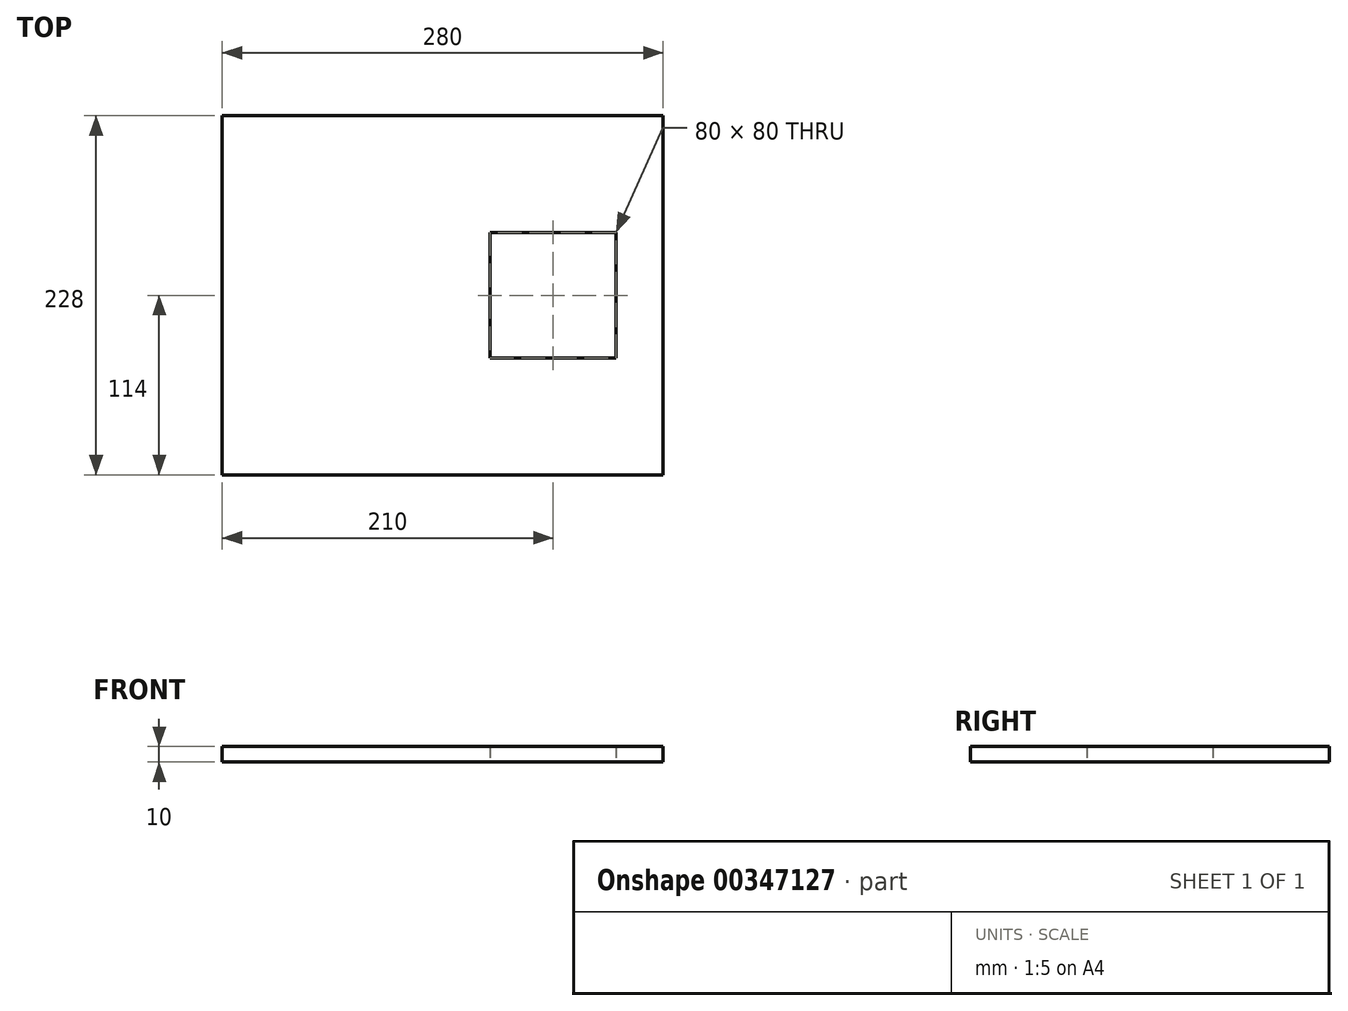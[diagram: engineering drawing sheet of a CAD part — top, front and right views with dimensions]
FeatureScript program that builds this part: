
annotation { "Feature Type Name" : "Feature", "Feature Type Description" : "" }
export const myFeature = defineFeature(function(context is Context, id is Id, definition is map)
    precondition{}
    {
        {
            var Q0;
            Q0=qCreatedBy(makeId("Top.planeOp"),FACE);
            var sketch = newSketch(context, id + "F0", { "sketchPlane" : qUnion([Q0])});
            skLineSegment(sketch, "E0.bottom", {"start": v(-140, 114) * mm, "end": v(140, 114) * mm});
            skLineSegment(sketch, "E0.top", {"start": v(-140, -114) * mm, "end": v(140, -114) * mm});
            skLineSegment(sketch, "E0.left", {"start": v(-140, 114) * mm, "end": v(-140, -114) * mm});
            skLineSegment(sketch, "E0.right", {"start": v(140, 114) * mm, "end": v(140, -114) * mm});
            skPoint(sketch, "E0.middle", {"position": v(0, 0) * mm});
            skPoint(sketch, "E1.visualSharp", {"position": v(-140, 114) * mm});
            skLineSegment(sketch, "E1.filletArc", {"start": v(-140, 114) * mm, "end": v(-140, 114) * mm});
            skPoint(sketch, "E2.visualSharp", {"position": v(140, 114) * mm});
            skLineSegment(sketch, "E2.filletArc", {"start": v(140, 114) * mm, "end": v(140, 114) * mm});
            skPoint(sketch, "E3.visualSharp", {"position": v(140, -114) * mm});
            skLineSegment(sketch, "E3.filletArc", {"start": v(140, -114) * mm, "end": v(140, -114) * mm});
            skPoint(sketch, "E4.visualSharp", {"position": v(-140, -114) * mm});
            skLineSegment(sketch, "E4.filletArc", {"start": v(-140, -114) * mm, "end": v(-140, -114) * mm});
            skLineSegment(sketch, "E5.bottom", {"start": v(30, 40) * mm, "end": v(110, 40) * mm});
            skLineSegment(sketch, "E5.top", {"start": v(30, -40) * mm, "end": v(110, -40) * mm});
            skLineSegment(sketch, "E5.left", {"start": v(30, 40) * mm, "end": v(30, -40) * mm});
            skLineSegment(sketch, "E5.right", {"start": v(110, 40) * mm, "end": v(110, -40) * mm});
            skPoint(sketch, "E5.middle", {"position": v(70, 0) * mm});
            skSolve(sketch);
        }
        {
            var Q0;
            Q0=qSketchRegion(id+"F0",true);
            extrude(context, id + "F1", {"entities" : qUnion([Q0]), "depth" : 10 * mm});
        }
    });
